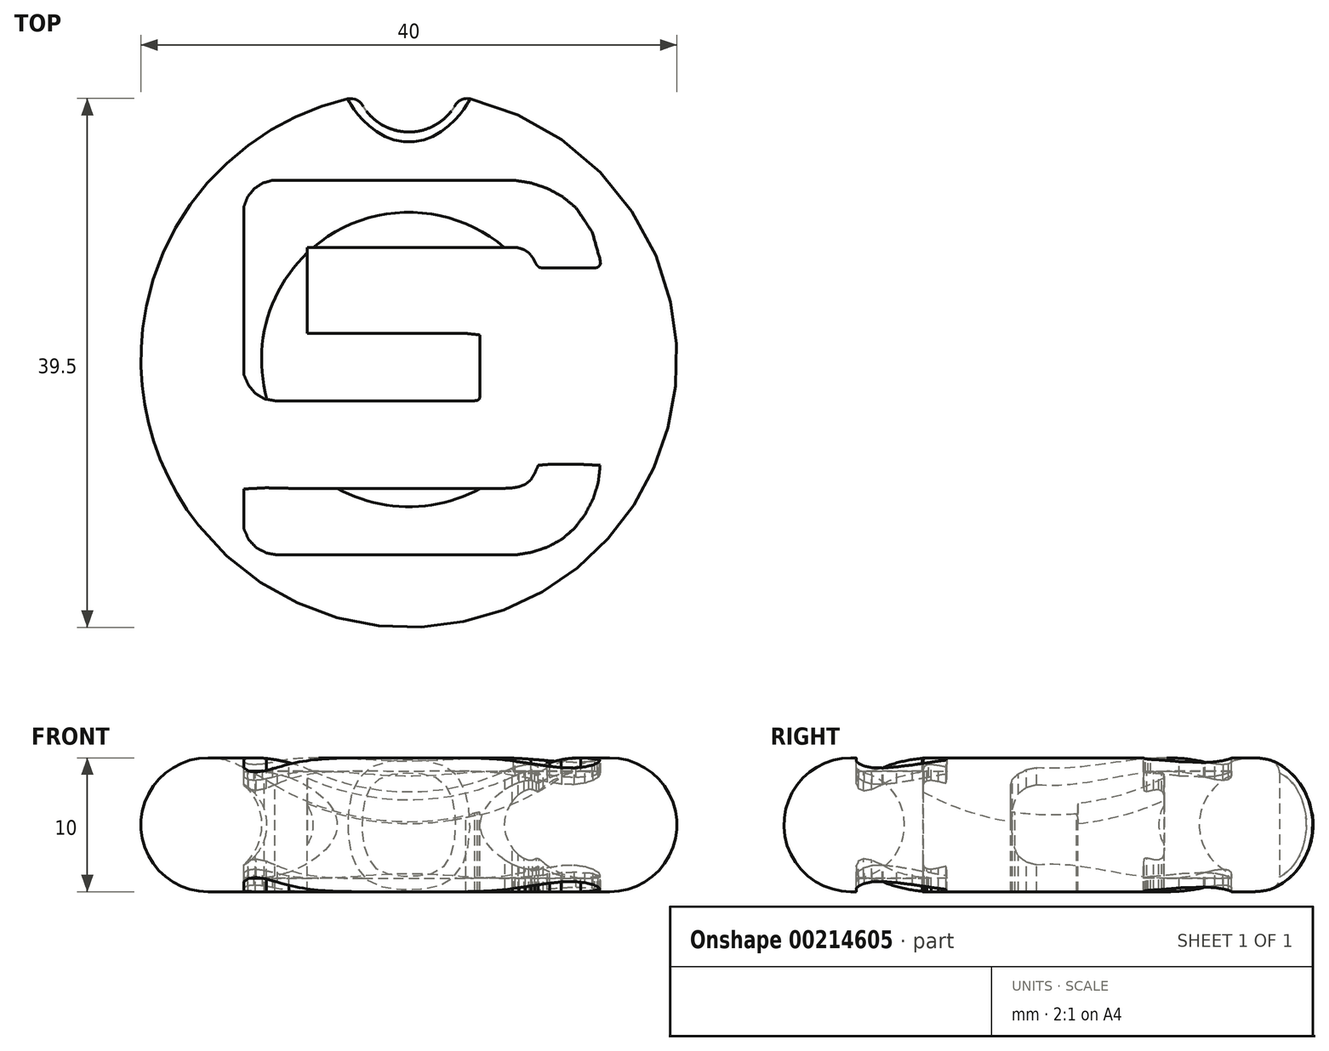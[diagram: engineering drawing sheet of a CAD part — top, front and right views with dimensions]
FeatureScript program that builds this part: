
annotation { "Feature Type Name" : "Feature", "Feature Type Description" : "" }
export const myFeature = defineFeature(function(context is Context, id is Id, definition is map)
    precondition{}
    {
        {
            var Q0;
            Q0=qCreatedBy(makeId("Front.planeOp"),FACE);
            var sketch = newSketch(context, id + "F0", { "sketchPlane" : qUnion([Q0])});
            skArc(sketch, "E0", {"start": v(-12, 9) * mm, "mid": v(-6.32, 6.03) * mm, "end": v(0, 5) * mm});
            skArc(sketch, "E1", {"start": v(-12, 9) * mm, "mid": v(-19.74, 6.58) * mm, "end": v(-15, 0) * mm});
            skLineSegment(sketch, "E2", {"start": v(-15, 0) * mm, "end": v(0, 0) * mm});
            skLineSegment(sketch, "E3", {"start": v(0, 0) * mm, "end": v(0, 5) * mm});
            skSolve(sketch);
        }
        {
            var Q0;
            Q0=makeQuery(id+"F0.imprint","IMPRINT",FACE,{"disambiguationData":[TD([[makeQuery(id+"F0.imprint","IMPRINT",EDGE,{"derivedFrom":sQuery(id+"F0.wireOp",EDGE,"E0")}),-1.0]])]});
            var Q1;
            Q1=sQuery(id+"F0.wireOp",EDGE,"E3");
            revolve(context, id + "F1", {"entities" : qUnion([Q0]), "axis" : qUnion([Q1]), "revolveType" : RevolveType.FULL});
        }
        {
            var Q0;
            Q0=qCreatedBy(makeId("Top.planeOp"),FACE);
            cPlane(context, id + "F2", {"entities" : qUnion([Q0]), "cplaneType" : CPlaneType.OFFSET, "offset" : 10 * mm, "width" : 150 * mm, "height" : 150 * mm});
        }
        {
            var Q0;
            Q0=qCreatedBy(id+"F2.planeOp",FACE);
            var sketch = newSketch(context, id + "F3", { "sketchPlane" : qUnion([Q0])});
            skLineSegment(sketch, "E4", {"start": v(7.95, -14.6) * mm, "end": v(-9.8, -14.6) * mm});
            skLineSegment(sketch, "E5", {"start": v(-9.8, -14.6) * mm, "end": v(-10.64, -14.45) * mm});
            skLineSegment(sketch, "E6", {"start": v(-10.64, -14.45) * mm, "end": v(-11.39, -14.05) * mm});
            skLineSegment(sketch, "E7", {"start": v(-11.39, -14.05) * mm, "end": v(-11.97, -13.45) * mm});
            skLineSegment(sketch, "E8", {"start": v(-11.97, -13.45) * mm, "end": v(-12.3, -12.66) * mm});
            skLineSegment(sketch, "E9", {"start": v(-12.3, -12.66) * mm, "end": v(-12.3, -9.67) * mm});
            skLineSegment(sketch, "E10", {"start": v(-12.3, -9.67) * mm, "end": v(-10.64, -9.58) * mm});
            skLineSegment(sketch, "E11", {"start": v(-10.64, -9.58) * mm, "end": v(-8.97, -9.62) * mm});
            skLineSegment(sketch, "E12", {"start": v(-8.97, -9.62) * mm, "end": v(7.19, -9.62) * mm});
            skLineSegment(sketch, "E13", {"start": v(7.19, -9.62) * mm, "end": v(7.7, -9.6) * mm});
            skLineSegment(sketch, "E14", {"start": v(7.7, -9.6) * mm, "end": v(8.22, -9.5) * mm});
            skLineSegment(sketch, "E15", {"start": v(8.22, -9.5) * mm, "end": v(8.7, -9.32) * mm});
            skLineSegment(sketch, "E16", {"start": v(8.7, -9.32) * mm, "end": v(9.1, -9) * mm});
            skLineSegment(sketch, "E17", {"start": v(9.1, -9) * mm, "end": v(9.41, -8.46) * mm});
            skLineSegment(sketch, "E18", {"start": v(9.41, -8.46) * mm, "end": v(9.66, -7.9) * mm});
            skLineSegment(sketch, "E19", {"start": v(9.66, -7.9) * mm, "end": v(10.51, -7.83) * mm});
            skLineSegment(sketch, "E20", {"start": v(10.51, -7.83) * mm, "end": v(11.37, -7.83) * mm});
            skLineSegment(sketch, "E21", {"start": v(11.37, -7.83) * mm, "end": v(12.82, -7.83) * mm});
            skLineSegment(sketch, "E22", {"start": v(12.82, -7.83) * mm, "end": v(14.28, -7.9) * mm});
            skLineSegment(sketch, "E23", {"start": v(14.28, -7.9) * mm, "end": v(14.14, -9.18) * mm});
            skLineSegment(sketch, "E24", {"start": v(14.14, -9.18) * mm, "end": v(13.75, -10.42) * mm});
            skLineSegment(sketch, "E25", {"start": v(13.75, -10.42) * mm, "end": v(13.15, -11.57) * mm});
            skLineSegment(sketch, "E26", {"start": v(13.15, -11.57) * mm, "end": v(12.36, -12.6) * mm});
            skLineSegment(sketch, "E27", {"start": v(12.36, -12.6) * mm, "end": v(11.43, -13.42) * mm});
            skLineSegment(sketch, "E28", {"start": v(11.43, -13.42) * mm, "end": v(10.35, -14) * mm});
            skLineSegment(sketch, "E29", {"start": v(10.35, -14) * mm, "end": v(9.17, -14.4) * mm});
            skLineSegment(sketch, "E30", {"start": v(9.17, -14.4) * mm, "end": v(7.95, -14.6) * mm});
            skLineSegment(sketch, "E31", {"start": v(5.31, -2.75) * mm, "end": v(5.26, -2.95) * mm});
            skLineSegment(sketch, "E32", {"start": v(5.26, -2.95) * mm, "end": v(5.1, -3.05) * mm});
            skLineSegment(sketch, "E33", {"start": v(5.1, -3.05) * mm, "end": v(4.9, -3.08) * mm});
            skLineSegment(sketch, "E34", {"start": v(4.9, -3.08) * mm, "end": v(4.7, -3.08) * mm});
            skLineSegment(sketch, "E35", {"start": v(4.7, -3.08) * mm, "end": v(-9.99, -3.08) * mm});
            skLineSegment(sketch, "E36", {"start": v(-9.99, -3.08) * mm, "end": v(-10.78, -2.94) * mm});
            skLineSegment(sketch, "E37", {"start": v(-10.78, -2.94) * mm, "end": v(-11.47, -2.52) * mm});
            skLineSegment(sketch, "E38", {"start": v(-11.47, -2.52) * mm, "end": v(-11.99, -1.9) * mm});
            skLineSegment(sketch, "E39", {"start": v(-11.99, -1.9) * mm, "end": v(-12.3, -1.15) * mm});
            skLineSegment(sketch, "E40", {"start": v(-12.3, -1.15) * mm, "end": v(-12.3, 11.45) * mm});
            skLineSegment(sketch, "E41", {"start": v(-12.3, 11.45) * mm, "end": v(-12.03, 12.17) * mm});
            skLineSegment(sketch, "E42", {"start": v(-12.03, 12.17) * mm, "end": v(-11.55, 12.77) * mm});
            skLineSegment(sketch, "E43", {"start": v(-11.55, 12.77) * mm, "end": v(-10.9, 13.19) * mm});
            skLineSegment(sketch, "E44", {"start": v(-10.9, 13.19) * mm, "end": v(-10.16, 13.4) * mm});
            skLineSegment(sketch, "E45", {"start": v(-10.16, 13.4) * mm, "end": v(7.82, 13.4) * mm});
            skLineSegment(sketch, "E46", {"start": v(7.82, 13.4) * mm, "end": v(9.1, 13.2) * mm});
            skLineSegment(sketch, "E47", {"start": v(9.1, 13.2) * mm, "end": v(10.33, 12.8) * mm});
            skLineSegment(sketch, "E48", {"start": v(10.33, 12.8) * mm, "end": v(11.47, 12.17) * mm});
            skLineSegment(sketch, "E49", {"start": v(11.47, 12.17) * mm, "end": v(12.47, 11.35) * mm});
            skLineSegment(sketch, "E50", {"start": v(12.47, 11.35) * mm, "end": v(13.7, 9.5) * mm});
            skLineSegment(sketch, "E51", {"start": v(13.7, 9.5) * mm, "end": v(14.3, 7.38) * mm});
            skLineSegment(sketch, "E52", {"start": v(14.3, 7.38) * mm, "end": v(14.3, 7.18) * mm});
            skLineSegment(sketch, "E53", {"start": v(14.3, 7.18) * mm, "end": v(14.23, 7) * mm});
            skLineSegment(sketch, "E54", {"start": v(14.23, 7) * mm, "end": v(14.08, 6.88) * mm});
            skLineSegment(sketch, "E55", {"start": v(14.08, 6.88) * mm, "end": v(13.87, 6.85) * mm});
            skLineSegment(sketch, "E56", {"start": v(13.87, 6.85) * mm, "end": v(10.02, 6.84) * mm});
            skLineSegment(sketch, "E57", {"start": v(10.02, 6.84) * mm, "end": v(9.73, 6.88) * mm});
            skLineSegment(sketch, "E58", {"start": v(9.73, 6.88) * mm, "end": v(9.53, 7.08) * mm});
            skLineSegment(sketch, "E59", {"start": v(9.53, 7.08) * mm, "end": v(9.39, 7.35) * mm});
            skLineSegment(sketch, "E60", {"start": v(9.39, 7.35) * mm, "end": v(9.25, 7.6) * mm});
            skLineSegment(sketch, "E61", {"start": v(9.25, 7.6) * mm, "end": v(8.97, 7.97) * mm});
            skLineSegment(sketch, "E62", {"start": v(8.97, 7.97) * mm, "end": v(8.6, 8.21) * mm});
            skLineSegment(sketch, "E63", {"start": v(8.6, 8.21) * mm, "end": v(8.16, 8.35) * mm});
            skLineSegment(sketch, "E64", {"start": v(8.16, 8.35) * mm, "end": v(7.7, 8.39) * mm});
            skLineSegment(sketch, "E65", {"start": v(7.7, 8.39) * mm, "end": v(-7.57, 8.37) * mm});
            skLineSegment(sketch, "E66", {"start": v(-7.57, 8.37) * mm, "end": v(-7.58, 1.96) * mm});
            skLineSegment(sketch, "E67", {"start": v(-7.58, 1.96) * mm, "end": v(3.2, 1.95) * mm});
            skLineSegment(sketch, "E68", {"start": v(3.2, 1.95) * mm, "end": v(4.26, 1.96) * mm});
            skLineSegment(sketch, "E69", {"start": v(4.26, 1.96) * mm, "end": v(5.32, 1.84) * mm});
            skLineSegment(sketch, "E70", {"start": v(5.32, 1.84) * mm, "end": v(5.31, -2.75) * mm});
            skSolve(sketch);
        }
        {
            var Q0;
            Q0 = qSketchRegion(id + "F3", true);
            extrude(context, id + "F4", {"entities" : qUnion([Q0]), "operationType" : NewBodyOperationType.REMOVE, "oppositeDirection" : true, "depth" : 25 * mm});
        }
        {
            var Q0;
            Q0=qCreatedBy(makeId("Front.planeOp"),FACE);
            var sketch = newSketch(context, id + "F5", { "sketchPlane" : qUnion([Q0])});
            skCircle(sketch, "E71", {"center": v(-15, 5) * mm, "radius": 4 * mm});
            skSolve(sketch);
        }
        {
            var Q0;
            Q0 = qSketchRegion(id + "F5", true);
            var Q1;
            Q1=sQuery(id+"F0.wireOp",EDGE,"E3");
            revolve(context, id + "F6", {"operationType" : NewBodyOperationType.ADD, "entities" : qUnion([Q0]), "axis" : qUnion([Q1]), "revolveType" : RevolveType.FULL});
        }
        {
            var Q0;
            Q0=qCreatedBy(makeId("Top.planeOp"),FACE);
            var sketch = newSketch(context, id + "F7", { "sketchPlane" : qUnion([Q0])});
            skCircle(sketch, "E72", {"center": v(0, 21) * mm, "radius": 4 * mm});
            skSolve(sketch);
        }
        {
            var Q0;
            Q0 = qSketchRegion(id + "F7", true);
            extrude(context, id + "F8", {"entities" : qUnion([Q0]), "operationType" : NewBodyOperationType.REMOVE, "depth" : 25 * mm});
        }
        {
            var Q0;
            Q0=makeQuery(id+"F8.boolean.opBoolean","COPY",FACE,{"derivedFrom":makeQuery(id+"F8.opExtrude","SWEPT_FACE",FACE,{"disambiguationData":[OSD([sQuery(id+"F7.wireOp",EDGE,"E72")])]})});
            fillet(context, id + "F9", {"entities" : qUnion([Q0]), "radius" : 1 * mm, "tangentPropagation" : true, "allowEdgeOverflow" : false});
        }
    });
